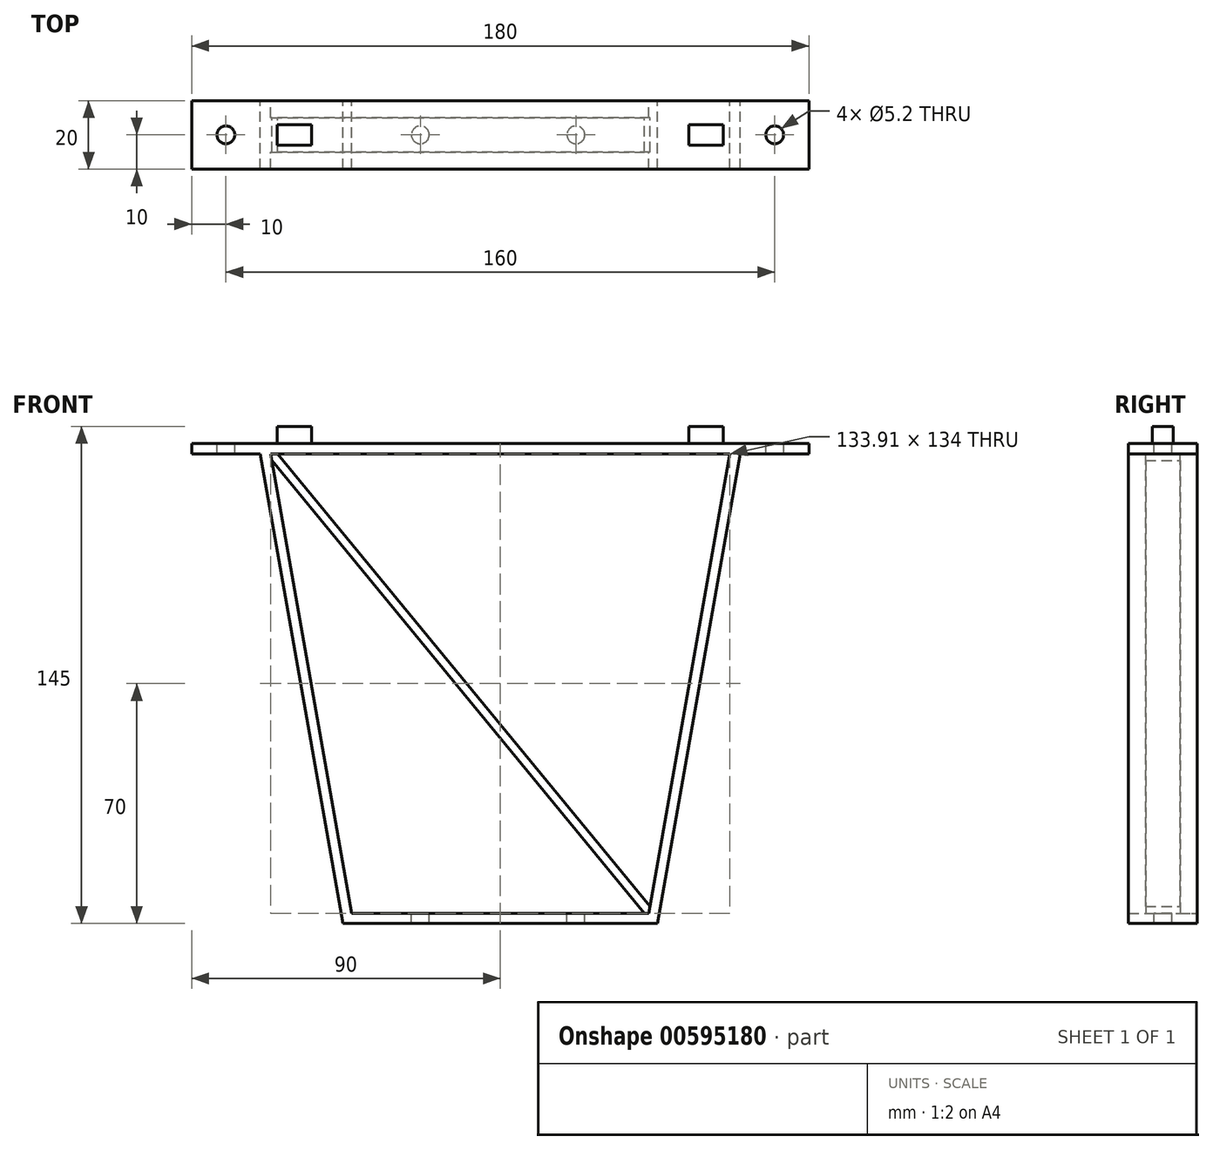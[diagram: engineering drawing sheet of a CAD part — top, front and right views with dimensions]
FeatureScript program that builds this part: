
annotation { "Feature Type Name" : "Feature", "Feature Type Description" : "" }
export const myFeature = defineFeature(function(context is Context, id is Id, definition is map)
    precondition{}
    {
        {
            var Q0;
            Q0=qCreatedBy(makeId("Front.planeOp"),FACE);
            var sketch = newSketch(context, id + "F0", { "sketchPlane" : qUnion([Q0])});
            skLineSegment(sketch, "E0", {"start": v(-90, 0) * mm, "end": v(90, 0) * mm});
            skLineSegment(sketch, "E1", {"start": v(90, 0) * mm, "end": v(90, -3) * mm});
            skLineSegment(sketch, "E2", {"start": v(90, -3) * mm, "end": v(70, -3) * mm});
            skLineSegment(sketch, "E3", {"start": v(70, -3) * mm, "end": v(45.84, -140) * mm});
            skLineSegment(sketch, "E4", {"start": v(45.84, -140) * mm, "end": v(-45.84, -140) * mm});
            skLineSegment(sketch, "E5", {"start": v(-45.84, -140) * mm, "end": v(-70, -3) * mm});
            skLineSegment(sketch, "E6", {"start": v(-70, -3) * mm, "end": v(-90, -3) * mm});
            skLineSegment(sketch, "E7", {"start": v(-90, -3) * mm, "end": v(-90, 0) * mm});
            skLineSegment(sketch, "E8", {"start": v(-66.95, -3) * mm, "end": v(66.95, -3) * mm});
            skLineSegment(sketch, "E9", {"start": v(66.95, -3) * mm, "end": v(43.33, -137) * mm});
            skLineSegment(sketch, "E10", {"start": v(43.33, -137) * mm, "end": v(-43.33, -137) * mm});
            skLineSegment(sketch, "E11", {"start": v(-43.33, -137) * mm, "end": v(-66.95, -3) * mm});
            skLineSegment(sketch, "E12", {"start": v(-66.6, -5) * mm, "end": v(42.03, -137) * mm});
            skLineSegment(sketch, "E13", {"start": v(42.03, -137) * mm, "end": v(43.33, -137) * mm});
            skLineSegment(sketch, "E14", {"start": v(43.68, -135) * mm, "end": v(-64.95, -3) * mm});
            skLineSegment(sketch, "E15", {"start": v(-64.95, -3) * mm, "end": v(-66.95, -3) * mm});
            skSolve(sketch);
        }
        {
            var Q0;
            Q0=makeQuery(id+"F0.imprint","IMPRINT",FACE,{"disambiguationData":[TD([[makeQuery(id+"F0.imprint","IMPRINT",EDGE,{"derivedFrom":sQuery(id+"F0.wireOp",EDGE,"E0")}),-1.0]])]});
            extrude(context, id + "F1", {"entities" : qUnion([Q0]), "endBound" : BoundingType.SYMMETRIC, "depth" : 20 * mm, "offsetDistance" : 25 * mm});
        }
        {
            var Q0;
            Q0=makeQuery(id+"F1.opExtrude","SWEPT_FACE",FACE,{"disambiguationData":[OSD([sQuery(id+"F0.wireOp",EDGE,"E0")])]});
            var sketch = newSketch(context, id + "F2", { "sketchPlane" : qUnion([Q0])});
            skLineSegment(sketch, "E16.bottom", {"start": v(-65, 3) * mm, "end": v(-55, 3) * mm});
            skLineSegment(sketch, "E16.top", {"start": v(-65, -3) * mm, "end": v(-55, -3) * mm});
            skLineSegment(sketch, "E16.left", {"start": v(-65, 3) * mm, "end": v(-65, -3) * mm});
            skLineSegment(sketch, "E16.right", {"start": v(-55, 3) * mm, "end": v(-55, -3) * mm});
            skCircle(sketch, "E17", {"center": v(-80, 0) * mm, "radius": 2.6 * mm});
            skCircle(sketch, "E18", {"center": v(80, 0) * mm, "radius": 2.6 * mm});
            skLineSegment(sketch, "E19.bottom", {"start": v(65, 3) * mm, "end": v(55, 3) * mm});
            skLineSegment(sketch, "E19.top", {"start": v(65, -3) * mm, "end": v(55, -3) * mm});
            skLineSegment(sketch, "E19.left", {"start": v(65, 3) * mm, "end": v(65, -3) * mm});
            skLineSegment(sketch, "E19.right", {"start": v(55, 3) * mm, "end": v(55, -3) * mm});
            skLineSegment(sketch, "E20", {"start": v(-65, 0) * mm, "end": v(-55, 0) * mm, "construction": true});
            skLineSegment(sketch, "E21", {"start": v(55, 0) * mm, "end": v(65, 0) * mm, "construction": true});
            skSolve(sketch);
        }
        {
            var Q0;
            Q0=makeQuery(id+"F2.imprint","IMPRINT",FACE,{"disambiguationData":[TD([[makeQuery(id+"F2.imprint","IMPRINT",EDGE,{"derivedFrom":sQuery(id+"F2.wireOp",EDGE,"E16.bottom")}),-1.0]])]});
            var Q1;
            Q1=makeQuery(id+"F2.imprint","IMPRINT",FACE,{"disambiguationData":[TD([[makeQuery(id+"F2.imprint","IMPRINT",EDGE,{"derivedFrom":sQuery(id+"F2.wireOp",EDGE,"E19.bottom")}),1.0]])]});
            extrude(context, id + "F3", {"entities" : qUnion([Q0, Q1]), "operationType" : NewBodyOperationType.ADD, "depth" : 5 * mm, "offsetDistance" : 25 * mm});
        }
        {
            var Q0;
            Q0=makeQuery(id+"F2.imprint","IMPRINT",FACE,{"disambiguationData":[TD([[makeQuery(id+"F2.imprint","IMPRINT",EDGE,{"derivedFrom":sQuery(id+"F2.wireOp",EDGE,"E17")}),1.0]])]});
            var Q1;
            Q1=makeQuery(id+"F2.imprint","IMPRINT",FACE,{"disambiguationData":[TD([[makeQuery(id+"F2.imprint","IMPRINT",EDGE,{"derivedFrom":sQuery(id+"F2.wireOp",EDGE,"E18")}),1.0]])]});
            var Q2;
            Q2=sQuery(id+"F2.wireOp",EDGE,"E17");
            extrude(context, id + "F4", {"entities" : qUnion([Q0, Q1]), "operationType" : NewBodyOperationType.REMOVE, "surfaceEntities" : qUnion([Q2]), "endBound" : BoundingType.UP_TO_NEXT, "oppositeDirection" : true, "depth" : 25 * mm, "offsetDistance" : 25 * mm});
        }
        {
            var Q0;
            Q0=makeQuery(id+"F1.opExtrude","SWEPT_FACE",FACE,{"disambiguationData":[OSD([sQuery(id+"F0.wireOp",EDGE,"E10")])]});
            var sketch = newSketch(context, id + "F5", { "sketchPlane" : qUnion([Q0])});
            skCircle(sketch, "E22", {"center": v(-23.33, 0) * mm, "radius": 2.6 * mm});
            skCircle(sketch, "E23", {"center": v(22.03, 0) * mm, "radius": 2.6 * mm});
            skSolve(sketch);
        }
        {
            var Q0;
            Q0 = qSketchRegion(id + "F5", true);
            extrude(context, id + "F6", {"entities" : qUnion([Q0]), "operationType" : NewBodyOperationType.REMOVE, "endBound" : BoundingType.UP_TO_NEXT, "oppositeDirection" : true, "depth" : 25 * mm, "offsetDistance" : 25 * mm});
        }
        {
            var Q0;
            {var subQ0=sQuery(id+"F0.wireOp",EDGE,"E12");Q0=makeQuery(id+"F0.imprint","IMPRINT",FACE,{"disambiguationData":[TD([[makeQuery(id+"F0.imprint","IMPRINT",EDGE,{"derivedFrom":subQ0}),1.0]])]});}
            var Q1;
            Q1=sQuery(id+"F0.wireOp",EDGE,"E14");
            var Q2;
            Q2=sQuery(id+"F0.wireOp",EDGE,"E12");
            extrude(context, id + "F7", {"entities" : qUnion([Q0]), "operationType" : NewBodyOperationType.ADD, "surfaceEntities" : qUnion([Q1, Q2]), "endBound" : BoundingType.SYMMETRIC, "depth" : 10 * mm, "offsetDistance" : 25 * mm});
        }
    });
